# Revit family: Клапан регулирующий ВКТР с аналоговым ВЭП DN15-300, PN16
name_source: partatom
category: Арматура трубопроводов
revit_build: Autodesk Revit 2015 (Build: 20140322_1515(x64)
units: mm (PartAtom-declared; Revit-internal decimal feet)

## types (72) — shared parameters
URL = http://vogez.by
Видимость клапана = Да
Высота болтов площадки = 6 мм
Высота штока_1 = 25 мм
Высота штока_2 = 100 мм
Диаметр направляющих = 10 мм
Диаметр отверстий = 65 мм
Диаметр площадки привода_2 = 35 мм
Диаметр присоединения привода = 40 мм
Диаметр присоединения провода = 15 мм
Диаметр штока_1 = 30 мм
Диаметр штока_2 = 8 мм
Изготовитель = ООО "ВОГЕЗЭНЕРГО"
Максимальная температура среды = 150 °C
Материал и цвет клапана = Чугун, серый
Материал и цвет остальных элементов = Сталь, полированная
Материал и цвет привода = Пластик, чёрный
Наименование = Клапан трёхходовой регулирующий с ЭИМ
Номинальное давление PN = 1.6 МПа
Основание пластины = 20 мм
Рабочая среда = вода
Расстояние до оси привода_1 = 42 мм
Расстояние до оси привода_2 = 133 мм
Сигнал управления = аналоговый
Скругления привода = 25 мм
Степень защиты = IP54
Толщиина пластины = 5 мм
Частота сети = 50 Гц
Ширина пластины = 30 мм
Ширина площадки = 20 мм
Ширина привода = 112 мм

## per-type parameters (varying)
- Клапан регулирующий ВКТР с ЭИМ DN15, Kvy=0.63 м3/ч, 220В: DN=15 мм; Высота клапана=65 мм; Высота направляющих=185 мм; Высота основания привода=195 мм; Высота посадки привода=45 мм; Высота с приводом=265 мм; Диаметр зеркала=51 мм; Диаметр патрубка_1=40 мм; Диаметр патрубка_2=40 мм; Диаметр площадки привода_1=80 мм; Диаметр узла смешивания=70 мм; Диаметр условный DN=15 мм; Диаметр фланца=100 мм; Длина пластины=112 мм; Длина площадки=60 мм; Исполнение ВЭП=1; Масса с приводом=7.00 kg; Межосевое направляющих=65 мм; Напряжение питания=220 В; Номинальное время полного хода ВЭП=63 с; Номинальное усилие ВЭП=1500 Н; Номинальный полный ход ВЭП=20 мм; Обозначение=ВКТР DN15-03 c ЭИМ Kv 0.63; Радиус зеркала=26 мм; Радиус условный=8 мм; Радиус фланца=50 мм; Строительная длина=130 мм; Тип привода=ВЭП-138-1500/63-20; Тип, марка=ВКТР DN15-03 c ЭИМ Kv 0.63; Толщина зеркала=2 мм; Толщина фланца=12 мм; Условная пропускная способность Kvy=0.6 м³/ч; Ход штока=14 мм
- Клапан регулирующий ВКТР с ЭИМ DN15, Kvy=1.25 м3/ч, 220В: DN=15 мм; Высота клапана=65 мм; Высота направляющих=185 мм; Высота основания привода=195 мм; Высота посадки привода=45 мм; Высота с приводом=265 мм; Диаметр зеркала=51 мм; Диаметр патрубка_1=40 мм; Диаметр патрубка_2=40 мм; Диаметр площадки привода_1=80 мм; Диаметр узла смешивания=70 мм; Диаметр условный DN=15 мм; Диаметр фланца=100 мм; Длина пластины=112 мм; Длина площадки=60 мм; Исполнение ВЭП=1; Масса с приводом=7.00 kg; Межосевое направляющих=65 мм; Напряжение питания=220 В; Номинальное время полного хода ВЭП=63 с; Номинальное усилие ВЭП=1500 Н; Номинальный полный ход ВЭП=20 мм; Обозначение=ВКТР DN15-03 c ЭИМ Kv 1.25; Радиус зеркала=26 мм; Радиус условный=8 мм; Радиус фланца=50 мм; Строительная длина=130 мм; Тип привода=ВЭП-138-1500/63-20; Тип, марка=ВКТР DN15-03 c ЭИМ Kv 1.25; Толщина зеркала=2 мм; Толщина фланца=12 мм; Условная пропускная способность Kvy=1.3 м³/ч; Ход штока=14 мм
- Клапан регулирующий ВКТР с ЭИМ DN15, Kvy=1.6 м3/ч, 220В: DN=15 мм; Высота клапана=65 мм; Высота направляющих=185 мм; Высота основания привода=195 мм; Высота посадки привода=45 мм; Высота с приводом=265 мм; Диаметр зеркала=51 мм; Диаметр патрубка_1=40 мм; Диаметр патрубка_2=40 мм; Диаметр площадки привода_1=80 мм; Диаметр узла смешивания=70 мм; Диаметр условный DN=15 мм; Диаметр фланца=100 мм; Длина пластины=112 мм; Длина площадки=60 мм; Исполнение ВЭП=1; Масса с приводом=7.00 kg; Межосевое направляющих=65 мм; Напряжение питания=220 В; Номинальное время полного хода ВЭП=63 с; Номинальное усилие ВЭП=1500 Н; Номинальный полный ход ВЭП=20 мм; Обозначение=ВКТР DN15-03 c ЭИМ Kv 1.6; Радиус зеркала=26 мм; Радиус условный=8 мм; Радиус фланца=50 мм; Строительная длина=130 мм; Тип привода=ВЭП-138-1500/63-20; Тип, марка=ВКТР DN15-03 c ЭИМ Kv 1.6; Толщина зеркала=2 мм; Толщина фланца=12 мм; Условная пропускная способность Kvy=1.6 м³/ч; Ход штока=14 мм
- Клапан регулирующий ВКТР с ЭИМ DN15, Kvy=2.5 м3/ч, 220В: DN=15 мм; Высота клапана=65 мм; Высота направляющих=185 мм; Высота основания привода=195 мм; Высота посадки привода=45 мм; Высота с приводом=265 мм; Диаметр зеркала=51 мм; Диаметр патрубка_1=40 мм; Диаметр патрубка_2=40 мм; Диаметр площадки привода_1=80 мм; Диаметр узла смешивания=70 мм; Диаметр условный DN=15 мм; Диаметр фланца=100 мм; Длина пластины=112 мм; Длина площадки=60 мм; Исполнение ВЭП=1; Масса с приводом=7.00 kg; Межосевое направляющих=65 мм; Напряжение питания=220 В; Номинальное время полного хода ВЭП=63 с; Номинальное усилие ВЭП=1500 Н; Номинальный полный ход ВЭП=20 мм; Обозначение=ВКТР DN15-03 c ЭИМ Kv 2.5; Радиус зеркала=26 мм; Радиус условный=8 мм; Радиус фланца=50 мм; Строительная длина=130 мм; Тип привода=ВЭП-138-1500/63-20; Тип, марка=ВКТР DN15-03 c ЭИМ Kv 2.5; Толщина зеркала=2 мм; Толщина фланца=12 мм; Условная пропускная способность Kvy=2.5 м³/ч; Ход штока=14 мм
- Клапан регулирующий ВКТР с ЭИМ DN15, Kvy=4 м3/ч, 220В: DN=15 мм; Высота клапана=65 мм; Высота направляющих=185 мм; Высота основания привода=195 мм; Высота посадки привода=45 мм; Высота с приводом=265 мм; Диаметр зеркала=51 мм; Диаметр патрубка_1=40 мм; Диаметр патрубка_2=40 мм; Диаметр площадки привода_1=80 мм; Диаметр узла смешивания=70 мм; Диаметр условный DN=15 мм; Диаметр фланца=100 мм; Длина пластины=112 мм; Длина площадки=60 мм; Исполнение ВЭП=1; Масса с приводом=7.00 kg; Межосевое направляющих=65 мм; Напряжение питания=220 В; Номинальное время полного хода ВЭП=63 с; Номинальное усилие ВЭП=1500 Н; Номинальный полный ход ВЭП=20 мм; Обозначение=ВКТР DN15-03 c ЭИМ Kv 4; Радиус зеркала=26 мм; Радиус условный=8 мм; Радиус фланца=50 мм; Строительная длина=130 мм; Тип привода=ВЭП-138-1500/63-20; Тип, марка=ВКТР DN15-03 c ЭИМ Kv 4; Толщина зеркала=2 мм; Толщина фланца=12 мм; Условная пропускная способность Kvy=4.0 м³/ч; Ход штока=14 мм
- Клапан регулирующий ВКТР с ЭИМ DN20, Kvy=5 м3/ч, 220В: DN=20 мм; Высота клапана=70 мм; Высота направляющих=195 мм; Высота основания привода=205 мм; Высота посадки привода=55 мм; Высота с приводом=275 мм; Диаметр зеркала=60 мм; Диаметр патрубка_1=45 мм; Диаметр патрубка_2=40 мм; Диаметр площадки привода_1=80 мм; Диаметр узла смешивания=90 мм; Диаметр условный DN=20 мм; Диаметр фланца=110 мм; Длина пластины=112 мм; Длина площадки=80 мм; Исполнение ВЭП=1; Масса с приводом=8.00 kg; Межосевое направляющих=65 мм; Напряжение питания=220 В; Номинальное время полного хода ВЭП=63 с; Номинальное усилие ВЭП=1500 Н; Номинальный полный ход ВЭП=20 мм; Обозначение=ВКТР DN20-03 c ЭИМ Kv 5; Радиус зеркала=30 мм; Радиус условный=10 мм; Радиус фланца=55 мм; Строительная длина=150 мм; Тип привода=ВЭП-138-1500/63-20; Тип, марка=ВКТР DN20-03 c ЭИМ Kv 5; Толщина зеркала=2 мм; Толщина фланца=14 мм; Условная пропускная способность Kvy=5.0 м³/ч; Ход штока=14 мм
- Клапан регулирующий ВКТР с ЭИМ DN20, Kvy=6.3 м3/ч, 220В: DN=20 мм; Высота клапана=70 мм; Высота направляющих=195 мм; Высота основания привода=205 мм; Высота посадки привода=55 мм; Высота с приводом=275 мм; Диаметр зеркала=60 мм; Диаметр патрубка_1=45 мм; Диаметр патрубка_2=40 мм; Диаметр площадки привода_1=80 мм; Диаметр узла смешивания=90 мм; Диаметр условный DN=20 мм; Диаметр фланца=110 мм; Длина пластины=112 мм; Длина площадки=80 мм; Исполнение ВЭП=1; Масса с приводом=8.00 kg; Межосевое направляющих=65 мм; Напряжение питания=220 В; Номинальное время полного хода ВЭП=63 с; Номинальное усилие ВЭП=1500 Н; Номинальный полный ход ВЭП=20 мм; Обозначение=ВКТР DN20-03 c ЭИМ Kv 6.3; Радиус зеркала=30 мм; Радиус условный=10 мм; Радиус фланца=55 мм; Строительная длина=150 мм; Тип привода=ВЭП-138-1500/63-20; Тип, марка=ВКТР DN20-03 c ЭИМ Kv 6.3; Толщина зеркала=2 мм; Толщина фланца=14 мм; Условная пропускная способность Kvy=6.3 м³/ч; Ход штока=14 мм
- Клапан регулирующий ВКТР с ЭИМ DN25, Kvy=8 м3/ч, 220В: DN=25 мм; Высота клапана=75 мм; Высота направляющих=200 мм; Высота основания привода=210 мм; Высота посадки привода=60 мм; Высота с приводом=280 мм; Диаметр зеркала=71 мм; Диаметр патрубка_1=50 мм; Диаметр патрубка_2=40 мм; Диаметр площадки привода_1=80 мм; Диаметр узла смешивания=100 мм; Диаметр условный DN=25 мм; Диаметр фланца=120 мм; Длина пластины=112 мм; Длина площадки=90 мм; Исполнение ВЭП=1; Масса с приводом=9.00 kg; Межосевое направляющих=65 мм; Напряжение питания=220 В; Номинальное время полного хода ВЭП=63 с; Номинальное усилие ВЭП=1500 Н; Номинальный полный ход ВЭП=20 мм; Обозначение=ВКТР DN25-03 c ЭИМ Kv 8; Радиус зеркала=36 мм; Радиус условный=13 мм; Радиус фланца=60 мм; Строительная длина=160 мм; Тип привода=ВЭП-138-1500/63-20; Тип, марка=ВКТР DN25-03 c ЭИМ Kv 8; Толщина зеркала=2 мм; Толщина фланца=16 мм; Условная пропускная способность Kvy=8.0 м³/ч; Ход штока=14 мм
- Клапан регулирующий ВКТР с ЭИМ DN25, Kvy=10 м3/ч, 220В: DN=25 мм; Высота клапана=75 мм; Высота направляющих=200 мм; Высота основания привода=210 мм; Высота посадки привода=60 мм; Высота с приводом=280 мм; Диаметр зеркала=71 мм; Диаметр патрубка_1=50 мм; Диаметр патрубка_2=40 мм; Диаметр площадки привода_1=80 мм; Диаметр узла смешивания=100 мм; Диаметр условный DN=25 мм; Диаметр фланца=120 мм; Длина пластины=112 мм; Длина площадки=90 мм; Исполнение ВЭП=1; Масса с приводом=9.00 kg; Межосевое направляющих=65 мм; Напряжение питания=220 В; Номинальное время полного хода ВЭП=63 с; Номинальное усилие ВЭП=1500 Н; Номинальный полный ход ВЭП=20 мм; Обозначение=ВКТР DN25-03 c ЭИМ Kv 10; Радиус зеркала=36 мм; Радиус условный=13 мм; Радиус фланца=60 мм; Строительная длина=160 мм; Тип привода=ВЭП-138-1500/63-20; Тип, марка=ВКТР DN25-03 c ЭИМ Kv 10; Толщина зеркала=2 мм; Толщина фланца=16 мм; Условная пропускная способность Kvy=10.0 м³/ч; Ход штока=14 мм
- Клапан регулирующий ВКТР с ЭИМ DN32, Kvy=12.5 м3/ч, 220В: DN=32 мм; Высота клапана=95 мм; Высота направляющих=210 мм; Высота основания привода=220 мм; Высота посадки привода=70 мм; Высота с приводом=290 мм; Диаметр зеркала=82 мм; Диаметр патрубка_1=57 мм; Диаметр патрубка_2=40 мм; Диаметр площадки привода_1=80 мм; Диаметр узла смешивания=120 мм; Диаметр условный DN=32 мм; Диаметр фланца=135 мм; Длина пластины=112 мм; Длина площадки=110 мм; Исполнение ВЭП=1; Масса с приводом=11.00 kg; Межосевое направляющих=65 мм; Напряжение питания=220 В; Номинальное время полного хода ВЭП=63 с; Номинальное усилие ВЭП=1500 Н; Номинальный полный ход ВЭП=20 мм; Обозначение=ВКТР DN32-03 c ЭИМ Kv 12.5; Радиус зеркала=41 мм; Радиус условный=16 мм; Радиус фланца=68 мм; Строительная длина=180 мм; Тип привода=ВЭП-138-1500/63-20; Тип, марка=ВКТР DN32-03 c ЭИМ Kv 12.5; Толщина зеркала=2 мм; Толщина фланца=16 мм; Условная пропускная способность Kvy=12.5 м³/ч; Ход штока=14 мм
- Клапан регулирующий ВКТР с ЭИМ DN32, Kvy=16 м3/ч, 220В: DN=32 мм; Высота клапана=95 мм; Высота направляющих=210 мм; Высота основания привода=220 мм; Высота посадки привода=70 мм; Высота с приводом=290 мм; Диаметр зеркала=82 мм; Диаметр патрубка_1=57 мм; Диаметр патрубка_2=40 мм; Диаметр площадки привода_1=80 мм; Диаметр узла смешивания=120 мм; Диаметр условный DN=32 мм; Диаметр фланца=135 мм; Длина пластины=112 мм; Длина площадки=110 мм; Исполнение ВЭП=1; Масса с приводом=11.00 kg; Межосевое направляющих=65 мм; Напряжение питания=220 В; Номинальное время полного хода ВЭП=63 с; Номинальное усилие ВЭП=1500 Н; Номинальный полный ход ВЭП=20 мм; Обозначение=ВКТР DN32-03 c ЭИМ Kv 16; Радиус зеркала=41 мм; Радиус условный=16 мм; Радиус фланца=68 мм; Строительная длина=180 мм; Тип привода=ВЭП-138-1500/63-20; Тип, марка=ВКТР DN32-03 c ЭИМ Kv 16; Толщина зеркала=2 мм; Толщина фланца=16 мм; Условная пропускная способность Kvy=16.0 м³/ч; Ход штока=14 мм
- Клапан регулирующий ВКТР с ЭИМ DN40, Kvy=20 м3/ч, 220В: DN=40 мм; Высота клапана=100 мм; Высота направляющих=215 мм; Высота основания привода=225 мм; Высота посадки привода=75 мм; Высота с приводом=295 мм; Диаметр зеркала=92 мм; Диаметр патрубка_1=65 мм; Диаметр патрубка_2=60 мм; Диаметр площадки привода_1=80 мм; Диаметр узла смешивания=130 мм; Диаметр условный DN=40 мм; Диаметр фланца=145 мм; Длина пластины=112 мм; Длина площадки=120 мм; Исполнение ВЭП=1; Масса с приводом=13.00 kg; Межосевое направляющих=65 мм; Напряжение питания=220 В; Номинальное время полного хода ВЭП=63 с; Номинальное усилие ВЭП=1500 Н; Номинальный полный ход ВЭП=20 мм; Обозначение=ВКТР DN40-03 c ЭИМ Kv 20; Радиус зеркала=46 мм; Радиус условный=20 мм; Радиус фланца=73 мм; Строительная длина=200 мм; Тип привода=ВЭП-138-1500/63-20; Тип, марка=ВКТР DN40-03 c ЭИМ Kv 20; Толщина зеркала=3 мм; Толщина фланца=17 мм; Условная пропускная способность Kvy=20.0 м³/ч; Ход штока=14 мм
- Клапан регулирующий ВКТР с ЭИМ DN40, Kvy=25 м3/ч, 220В: DN=40 мм; Высота клапана=100 мм; Высота направляющих=215 мм; Высота основания привода=225 мм; Высота посадки привода=75 мм; Высота с приводом=295 мм; Диаметр зеркала=92 мм; Диаметр патрубка_1=65 мм; Диаметр патрубка_2=60 мм; Диаметр площадки привода_1=80 мм; Диаметр узла смешивания=130 мм; Диаметр условный DN=40 мм; Диаметр фланца=145 мм; Длина пластины=112 мм; Длина площадки=120 мм; Исполнение ВЭП=1; Масса с приводом=13.00 kg; Межосевое направляющих=65 мм; Напряжение питания=220 В; Номинальное время полного хода ВЭП=63 с; Номинальное усилие ВЭП=1500 Н; Номинальный полный ход ВЭП=20 мм; Обозначение=ВКТР DN40-03 c ЭИМ Kv 25; Радиус зеркала=46 мм; Радиус условный=20 мм; Радиус фланца=73 мм; Строительная длина=200 мм; Тип привода=ВЭП-138-1500/63-20; Тип, марка=ВКТР DN40-03 c ЭИМ Kv 25; Толщина зеркала=3 мм; Толщина фланца=17 мм; Условная пропускная способность Kvy=25.0 м³/ч; Ход штока=14 мм
- Клапан регулирующий ВКТР с ЭИМ DN50, Kvy=32 м3/ч, 220В: DN=50 мм; Высота клапана=100 мм; Высота направляющих=225 мм; Высота основания привода=235 мм; Высота посадки привода=85 мм; Высота с приводом=305 мм; Диаметр зеркала=107 мм; Диаметр патрубка_1=75 мм; Диаметр патрубка_2=60 мм; Диаметр площадки привода_1=80 мм; Диаметр узла смешивания=150 мм; Диаметр условный DN=50 мм; Диаметр фланца=160 мм; Длина пластины=112 мм; Длина площадки=140 мм; Исполнение ВЭП=1; Масса с приводом=15.00 kg; Межосевое направляющих=65 мм; Напряжение питания=220 В; Номинальное время полного хода ВЭП=63 с; Номинальное усилие ВЭП=1500 Н; Номинальный полный ход ВЭП=20 мм; Обозначение=ВКТР DN50-03 c ЭИМ Kv 32; Радиус зеркала=54 мм; Радиус условный=25 мм; Радиус фланца=80 мм; Строительная длина=230 мм; Тип привода=ВЭП-138-1500/63-20; Тип, марка=ВКТР DN50-03 c ЭИМ Kv 32; Толщина зеркала=3 мм; Толщина фланца=19 мм; Условная пропускная способность Kvy=32.0 м³/ч; Ход штока=14 мм
- Клапан регулирующий ВКТР с ЭИМ DN50, Kvy=40 м3/ч, 220В: DN=50 мм; Высота клапана=100 мм; Высота направляющих=225 мм; Высота основания привода=235 мм; Высота посадки привода=85 мм; Высота с приводом=305 мм; Диаметр зеркала=107 мм; Диаметр патрубка_1=75 мм; Диаметр патрубка_2=60 мм; Диаметр площадки привода_1=80 мм; Диаметр узла смешивания=150 мм; Диаметр условный DN=50 мм; Диаметр фланца=160 мм; Длина пластины=112 мм; Длина площадки=140 мм; Исполнение ВЭП=1; Масса с приводом=15.00 kg; Межосевое направляющих=65 мм; Напряжение питания=220 В; Номинальное время полного хода ВЭП=63 с; Номинальное усилие ВЭП=1500 Н; Номинальный полный ход ВЭП=20 мм; Обозначение=ВКТР DN50-03 c ЭИМ Kv 40; Радиус зеркала=54 мм; Радиус условный=25 мм; Радиус фланца=80 мм; Строительная длина=230 мм; Тип привода=ВЭП-138-1500/63-20; Тип, марка=ВКТР DN50-03 c ЭИМ Kv 40; Толщина зеркала=3 мм; Толщина фланца=19 мм; Условная пропускная способность Kvy=40.0 м³/ч; Ход штока=14 мм
- Клапан регулирующий ВКТР с ЭИМ DN65, Kvy=50 м3/ч, 220В: DN=65 мм; Высота клапана=120 мм; Высота направляющих=285 мм; Высота основания привода=295 мм; Высота посадки привода=115 мм; Высота с приводом=365 мм; Диаметр зеркала=127 мм; Диаметр патрубка_1=90 мм; Диаметр патрубка_2=60 мм; Диаметр площадки привода_1=80 мм; Диаметр узла смешивания=210 мм; Диаметр условный DN=65 мм; Диаметр фланца=180 мм; Длина пластины=112 мм; Длина площадки=200 мм; Исполнение ВЭП=1; Масса с приводом=24.00 kg; Межосевое направляющих=65 мм; Напряжение питания=220 В; Номинальное время полного хода ВЭП=100 с; Номинальное усилие ВЭП=3000 Н; Номинальный полный ход ВЭП=32 мм; Обозначение=ВКТР DN65-03 c ЭИМ Kv 50; Радиус зеркала=64 мм; Радиус условный=33 мм; Радиус фланца=90 мм; Строительная длина=290 мм; Тип привода=ВЭП-138-3000/100-32; Тип, марка=ВКТР DN65-03 c ЭИМ Kv 50; Толщина зеркала=3 мм; Толщина фланца=21 мм; Условная пропускная способность Kvy=50.0 м³/ч; Ход штока=30 мм
- Клапан регулирующий ВКТР с ЭИМ DN65, Kvy=63 м3/ч, 220В: DN=65 мм; Высота клапана=120 мм; Высота направляющих=285 мм; Высота основания привода=295 мм; Высота посадки привода=115 мм; Высота с приводом=365 мм; Диаметр зеркала=127 мм; Диаметр патрубка_1=90 мм; Диаметр патрубка_2=60 мм; Диаметр площадки привода_1=80 мм; Диаметр узла смешивания=210 мм; Диаметр условный DN=65 мм; Диаметр фланца=180 мм; Длина пластины=112 мм; Длина площадки=200 мм; Исполнение ВЭП=1; Масса с приводом=24.00 kg; Межосевое направляющих=65 мм; Напряжение питания=220 В; Номинальное время полного хода ВЭП=100 с; Номинальное усилие ВЭП=3000 Н; Номинальный полный ход ВЭП=32 мм; Обозначение=ВКТР DN65-03 c ЭИМ Kv 63; Радиус зеркала=64 мм; Радиус условный=33 мм; Радиус фланца=90 мм; Строительная длина=290 мм; Тип привода=ВЭП-138-3000/100-32; Тип, марка=ВКТР DN65-03 c ЭИМ Kv 63; Толщина зеркала=3 мм; Толщина фланца=21 мм; Условная пропускная способность Kvy=63.0 м³/ч; Ход штока=30 мм
- Клапан регулирующий ВКТР с ЭИМ DN80, Kvy=80 м3/ч, 220В: DN=80 мм; Высота клапана=130 мм; Высота направляющих=295 мм; Высота основания привода=305 мм; Высота посадки привода=125 мм; Высота с приводом=375 мм; Диаметр зеркала=139 мм; Диаметр патрубка_1=105 мм; Диаметр патрубка_2=60 мм; Диаметр площадки привода_1=80 мм; Диаметр узла смешивания=210 мм; Диаметр условный DN=80 мм; Диаметр фланца=195 мм; Длина пластины=112 мм; Длина площадки=200 мм; Исполнение ВЭП=1; Масса с приводом=28.00 kg; Межосевое направляющих=65 мм; Напряжение питания=220 В; Номинальное время полного хода ВЭП=100 с; Номинальное усилие ВЭП=3000 Н; Номинальный полный ход ВЭП=32 мм; Обозначение=ВКТР DN80-03 c ЭИМ Kv 80; Радиус зеркала=70 мм; Радиус условный=40 мм; Радиус фланца=98 мм; Строительная длина=310 мм; Тип привода=ВЭП-138-3000/100-32; Тип, марка=ВКТР DN80-03 c ЭИМ Kv 80; Толщина зеркала=3 мм; Толщина фланца=21 мм; Условная пропускная способность Kvy=80.0 м³/ч; Ход штока=30 мм
- Клапан регулирующий ВКТР с ЭИМ DN80, Kvy=100 м3/ч, 220В: DN=80 мм; Высота клапана=130 мм; Высота направляющих=295 мм; Высота основания привода=305 мм; Высота посадки привода=125 мм; Высота с приводом=375 мм; Диаметр зеркала=139 мм; Диаметр патрубка_1=105 мм; Диаметр патрубка_2=60 мм; Диаметр площадки привода_1=80 мм; Диаметр узла смешивания=210 мм; Диаметр условный DN=80 мм; Диаметр фланца=195 мм; Длина пластины=112 мм; Длина площадки=200 мм; Исполнение ВЭП=1; Масса с приводом=28.00 kg; Межосевое направляющих=65 мм; Напряжение питания=220 В; Номинальное время полного хода ВЭП=100 с; Номинальное усилие ВЭП=3000 Н; Номинальный полный ход ВЭП=32 мм; Обозначение=ВКТР DN80-03 c ЭИМ Kv 100; Радиус зеркала=70 мм; Радиус условный=40 мм; Радиус фланца=98 мм; Строительная длина=310 мм; Тип привода=ВЭП-138-3000/100-32; Тип, марка=ВКТР DN80-03 c ЭИМ Kv 100; Толщина зеркала=3 мм; Толщина фланца=21 мм; Условная пропускная способность Kvy=100.0 м³/ч; Ход штока=30 мм
- Клапан регулирующий ВКТР с ЭИМ DN100, Kvy=125 м3/ч, 220В: DN=100 мм; Высота клапана=150 мм; Высота направляющих=305 мм; Высота основания привода=315 мм; Высота посадки привода=135 мм; Высота с приводом=385 мм; Диаметр зеркала=162 мм; Диаметр патрубка_1=125 мм; Диаметр патрубка_2=70 мм; Диаметр площадки привода_1=80 мм; Диаметр узла смешивания=230 мм; Диаметр условный DN=100 мм; Диаметр фланца=215 мм; Длина пластины=112 мм; Длина площадки=220 мм; Исполнение ВЭП=1; Масса с приводом=40.00 kg; Межосевое направляющих=65 мм; Напряжение питания=220 В; Номинальное время полного хода ВЭП=100 с; Номинальное усилие ВЭП=3000 Н; Номинальный полный ход ВЭП=32 мм; Обозначение=ВКТР DN100-03 c ЭИМ Kv 125; Радиус зеркала=81 мм; Радиус условный=50 мм; Радиус фланца=108 мм; Строительная длина=350 мм; Тип привода=ВЭП-138-3000/100-32; Тип, марка=ВКТР DN100-03 c ЭИМ Kv 125; Толщина зеркала=3 мм; Толщина фланца=23 мм; Условная пропускная способность Kvy=125.0 м³/ч; Ход штока=30 мм
- Клапан регулирующий ВКТР с ЭИМ DN100, Kvy=160 м3/ч, 220В: DN=100 мм; Высота клапана=150 мм; Высота направляющих=305 мм; Высота основания привода=315 мм; Высота посадки привода=135 мм; Высота с приводом=385 мм; Диаметр зеркала=162 мм; Диаметр патрубка_1=125 мм; Диаметр патрубка_2=70 мм; Диаметр площадки привода_1=80 мм; Диаметр узла смешивания=230 мм; Диаметр условный DN=100 мм; Диаметр фланца=215 мм; Длина пластины=112 мм; Длина площадки=220 мм; Исполнение ВЭП=1; Масса с приводом=40.00 kg; Межосевое направляющих=65 мм; Напряжение питания=220 В; Номинальное время полного хода ВЭП=100 с; Номинальное усилие ВЭП=3000 Н; Номинальный полный ход ВЭП=32 мм; Обозначение=ВКТР DN100-03 c ЭИМ Kv 160; Радиус зеркала=81 мм; Радиус условный=50 мм; Радиус фланца=108 мм; Строительная длина=350 мм; Тип привода=ВЭП-138-3000/100-32; Тип, марка=ВКТР DN100-03 c ЭИМ Kv 160; Толщина зеркала=3 мм; Толщина фланца=23 мм; Условная пропускная способность Kvy=160.0 м³/ч; Ход штока=30 мм
- Клапан регулирующий ВКТР с ЭИМ DN125, Kvy=250 м3/ч, 220В: DN=125 мм; Высота клапана=160 мм; Высота направляющих=390 мм; Высота основания привода=400 мм; Высота посадки привода=90 мм; Высота с приводом=470 мм; Диаметр зеркала=190 мм; Диаметр патрубка_1=150 мм; Диаметр патрубка_2=100 мм; Диаметр площадки привода_1=130 мм; Диаметр узла смешивания=195 мм; Диаметр условный DN=125 мм; Диаметр фланца=245 мм; Длина пластины=130 мм; Длина площадки=185 мм; Исполнение ВЭП=1; Масса с приводом=64.00 kg; Межосевое направляющих=110 мм; Напряжение питания=220 В; Номинальное время полного хода ВЭП=100 с; Номинальное усилие ВЭП=4000 Н; Номинальный полный ход ВЭП=50 мм; Обозначение=ВКТР DN125-03 c ЭИМ Kv 250; Радиус зеркала=95 мм; Радиус условный=63 мм; Радиус фланца=123 мм; Строительная длина=400 мм; Тип привода=ВЭП-138-4000/100-50; Тип, марка=ВКТР DN125-03 c ЭИМ Kv 250; Толщина зеркала=3 мм; Толщина фланца=25 мм; Условная пропускная способность Kvy=250.0 м³/ч; Ход штока=50 мм
- Клапан регулирующий ВКТР с ЭИМ DN150, Kvy=315 м3/ч, 220В: DN=150 мм; Высота клапана=170 мм; Высота направляющих=410 мм; Высота основания привода=420 мм; Высота посадки привода=110 мм; Высота с приводом=490 мм; Диаметр зеркала=218 мм; Диаметр патрубка_1=175 мм; Диаметр патрубка_2=100 мм; Диаметр площадки привода_1=130 мм; Диаметр узла смешивания=235 мм; Диаметр условный DN=150 мм; Диаметр фланца=280 мм; Длина пластины=130 мм; Длина площадки=225 мм; Исполнение ВЭП=1; Масса с приводом=86.00 kg; Межосевое направляющих=110 мм; Напряжение питания=220 В; Номинальное время полного хода ВЭП=100 с; Номинальное усилие ВЭП=4000 Н; Номинальный полный ход ВЭП=50 мм; Обозначение=ВКТР DN150-03 c ЭИМ Kv 315; Радиус зеркала=109 мм; Радиус условный=75 мм; Радиус фланца=140 мм; Строительная длина=480 мм; Тип привода=ВЭП-138-4000/100-50; Тип, марка=ВКТР DN150-03 c ЭИМ Kv 315; Толщина зеркала=3 мм; Толщина фланца=25 мм; Условная пропускная способность Kvy=315.0 м³/ч; Ход штока=50 мм
- Клапан регулирующий ВКТР с ЭИМ DN200, Kvy=315 м3/ч, 220В: DN=200 мм; Высота клапана=400 мм; Высота направляющих=700 мм; Высота основания привода=710 мм; Высота посадки привода=350 мм; Высота с приводом=780 мм; Диаметр зеркала=274 мм; Диаметр патрубка_1=225 мм; Диаметр патрубка_2=100 мм; Диаметр площадки привода_1=130 мм; Диаметр узла смешивания=530 мм; Диаметр условный DN=200 мм; Диаметр фланца=335 мм; Длина пластины=130 мм; Длина площадки=520 мм; Исполнение ВЭП=1; Масса с приводом=240.00 kg; Межосевое направляющих=110 мм; Напряжение питания=220 В; Номинальное время полного хода ВЭП=160 с; Номинальное усилие ВЭП=10000 Н; Номинальный полный ход ВЭП=80 мм; Обозначение=ВКТР DN200-03 c ЭИМ Kv 315; Радиус зеркала=137 мм; Радиус условный=100 мм; Радиус фланца=168 мм; Строительная длина=600 мм; Тип привода=ВЭП-138-10000/160-80; Тип, марка=ВКТР DN200-03 c ЭИМ Kv 315; Толщина зеркала=3 мм; Толщина фланца=27 мм; Условная пропускная способность Kvy=315.0 м³/ч; Ход штока=60 мм
- Клапан регулирующий ВКТР с ЭИМ DN200, Kvy=400 м3/ч, 220В: DN=200 мм; Высота клапана=400 мм; Высота направляющих=700 мм; Высота основания привода=710 мм; Высота посадки привода=350 мм; Высота с приводом=780 мм; Диаметр зеркала=274 мм; Диаметр патрубка_1=225 мм; Диаметр патрубка_2=100 мм; Диаметр площадки привода_1=130 мм; Диаметр узла смешивания=530 мм; Диаметр условный DN=200 мм; Диаметр фланца=335 мм; Длина пластины=130 мм; Длина площадки=520 мм; Исполнение ВЭП=1; Масса с приводом=240.00 kg; Межосевое направляющих=110 мм; Напряжение питания=220 В; Номинальное время полного хода ВЭП=160 с; Номинальное усилие ВЭП=10000 Н; Номинальный полный ход ВЭП=80 мм; Обозначение=ВКТР DN200-03 c ЭИМ Kv 400; Радиус зеркала=137 мм; Радиус условный=100 мм; Радиус фланца=168 мм; Строительная длина=600 мм; Тип привода=ВЭП-138-10000/160-80; Тип, марка=ВКТР DN200-03 c ЭИМ Kv 400; Толщина зеркала=3 мм; Толщина фланца=27 мм; Условная пропускная способность Kvy=400.0 м³/ч; Ход штока=60 мм
- Клапан регулирующий ВКТР с ЭИМ DN200, Kvy=500 м3/ч, 220В: DN=200 мм; Высота клапана=400 мм; Высота направляющих=700 мм; Высота основания привода=710 мм; Высота посадки привода=350 мм; Высота с приводом=780 мм; Диаметр зеркала=274 мм; Диаметр патрубка_1=225 мм; Диаметр патрубка_2=100 мм; Диаметр площадки привода_1=130 мм; Диаметр узла смешивания=530 мм; Диаметр условный DN=200 мм; Диаметр фланца=335 мм; Длина пластины=130 мм; Длина площадки=520 мм; Исполнение ВЭП=1; Масса с приводом=240.00 kg; Межосевое направляющих=110 мм; Напряжение питания=220 В; Номинальное время полного хода ВЭП=160 с; Номинальное усилие ВЭП=10000 Н; Номинальный полный ход ВЭП=80 мм; Обозначение=ВКТР DN200-03 c ЭИМ Kv 500; Радиус зеркала=137 мм; Радиус условный=100 мм; Радиус фланца=168 мм; Строительная длина=600 мм; Тип привода=ВЭП-138-10000/160-80; Тип, марка=ВКТР DN200-03 c ЭИМ Kv 500; Толщина зеркала=3 мм; Толщина фланца=27 мм; Условная пропускная способность Kvy=500.0 м³/ч; Ход штока=60 мм
- Клапан регулирующий ВКТР с ЭИМ DN200, Kvy=630 м3/ч, 220В: DN=200 мм; Высота клапана=400 мм; Высота направляющих=700 мм; Высота основания привода=710 мм; Высота посадки привода=350 мм; Высота с приводом=780 мм; Диаметр зеркала=274 мм; Диаметр патрубка_1=225 мм; Диаметр патрубка_2=100 мм; Диаметр площадки привода_1=130 мм; Диаметр узла смешивания=530 мм; Диаметр условный DN=200 мм; Диаметр фланца=335 мм; Длина пластины=130 мм; Длина площадки=520 мм; Исполнение ВЭП=1; Масса с приводом=240.00 kg; Межосевое направляющих=110 мм; Напряжение питания=220 В; Номинальное время полного хода ВЭП=160 с; Номинальное усилие ВЭП=10000 Н; Номинальный полный ход ВЭП=80 мм; Обозначение=ВКТР DN200-03 c ЭИМ Kv 630; Радиус зеркала=137 мм; Радиус условный=100 мм; Радиус фланца=168 мм; Строительная длина=600 мм; Тип привода=ВЭП-138-10000/160-80; Тип, марка=ВКТР DN200-03 c ЭИМ Kv 630; Толщина зеркала=3 мм; Толщина фланца=27 мм; Условная пропускная способность Kvy=630.0 м³/ч; Ход штока=60 мм
- Клапан регулирующий ВКТР с ЭИМ DN250, Kvy=400 м3/ч, 220В: DN=250 мм; Высота клапана=450 мм; Высота направляющих=750 мм; Высота основания привода=760 мм; Высота посадки привода=400 мм; Высота с приводом=830 мм; Диаметр зеркала=326 мм; Диаметр патрубка_1=275 мм; Диаметр патрубка_2=100 мм; Диаметр площадки привода_1=130 мм; Диаметр узла смешивания=630 мм; Диаметр условный DN=250 мм; Диаметр фланца=405 мм; Длина пластины=130 мм; Длина площадки=620 мм; Исполнение ВЭП=1; Масса с приводом=300.00 kg; Межосевое направляющих=110 мм; Напряжение питания=220 В; Номинальное время полного хода ВЭП=160 с; Номинальное усилие ВЭП=10000 Н; Номинальный полный ход ВЭП=80 мм; Обозначение=ВКТР DN250-03 c ЭИМ Kv 400; Радиус зеркала=163 мм; Радиус условный=125 мм; Радиус фланца=203 мм; Строительная длина=730 мм; Тип привода=ВЭП-138-10000/160-80; Тип, марка=ВКТР DN250-03 c ЭИМ Kv 400; Толщина зеркала=3 мм; Толщина фланца=28 мм; Условная пропускная способность Kvy=400.0 м³/ч; Ход штока=80 мм
- Клапан регулирующий ВКТР с ЭИМ DN250, Kvy=500 м3/ч, 220В: DN=250 мм; Высота клапана=450 мм; Высота направляющих=750 мм; Высота основания привода=760 мм; Высота посадки привода=400 мм; Высота с приводом=830 мм; Диаметр зеркала=326 мм; Диаметр патрубка_1=275 мм; Диаметр патрубка_2=100 мм; Диаметр площадки привода_1=130 мм; Диаметр узла смешивания=630 мм; Диаметр условный DN=250 мм; Диаметр фланца=405 мм; Длина пластины=130 мм; Длина площадки=620 мм; Исполнение ВЭП=1; Масса с приводом=300.00 kg; Межосевое направляющих=110 мм; Напряжение питания=220 В; Номинальное время полного хода ВЭП=160 с; Номинальное усилие ВЭП=10000 Н; Номинальный полный ход ВЭП=80 мм; Обозначение=ВКТР DN250-03 c ЭИМ Kv 500; Радиус зеркала=163 мм; Радиус условный=125 мм; Радиус фланца=203 мм; Строительная длина=730 мм; Тип привода=ВЭП-138-10000/160-80; Тип, марка=ВКТР DN250-03 c ЭИМ Kv 500; Толщина зеркала=3 мм; Толщина фланца=28 мм; Условная пропускная способность Kvy=500.0 м³/ч; Ход штока=80 мм
- Клапан регулирующий ВКТР с ЭИМ DN250, Kvy=630 м3/ч, 220В: DN=250 мм; Высота клапана=450 мм; Высота направляющих=750 мм; Высота основания привода=760 мм; Высота посадки привода=400 мм; Высота с приводом=830 мм; Диаметр зеркала=326 мм; Диаметр патрубка_1=275 мм; Диаметр патрубка_2=100 мм; Диаметр площадки привода_1=130 мм; Диаметр узла смешивания=630 мм; Диаметр условный DN=250 мм; Диаметр фланца=405 мм; Длина пластины=130 мм; Длина площадки=620 мм; Исполнение ВЭП=1; Масса с приводом=300.00 kg; Межосевое направляющих=110 мм; Напряжение питания=220 В; Номинальное время полного хода ВЭП=160 с; Номинальное усилие ВЭП=10000 Н; Номинальный полный ход ВЭП=80 мм; Обозначение=ВКТР DN250-03 c ЭИМ Kv 630; Радиус зеркала=163 мм; Радиус условный=125 мм; Радиус фланца=203 мм; Строительная длина=730 мм; Тип привода=ВЭП-138-10000/160-80; Тип, марка=ВКТР DN250-03 c ЭИМ Kv 630; Толщина зеркала=3 мм; Толщина фланца=28 мм; Условная пропускная способность Kvy=630.0 м³/ч; Ход штока=80 мм
- Клапан регулирующий ВКТР с ЭИМ DN250, Kvy=800 м3/ч, 220В: DN=250 мм; Высота клапана=450 мм; Высота направляющих=750 мм; Высота основания привода=760 мм; Высота посадки привода=400 мм; Высота с приводом=830 мм; Диаметр зеркала=326 мм; Диаметр патрубка_1=275 мм; Диаметр патрубка_2=100 мм; Диаметр площадки привода_1=130 мм; Диаметр узла смешивания=630 мм; Диаметр условный DN=250 мм; Диаметр фланца=405 мм; Длина пластины=130 мм; Длина площадки=620 мм; Исполнение ВЭП=1; Масса с приводом=300.00 kg; Межосевое направляющих=110 мм; Напряжение питания=220 В; Номинальное время полного хода ВЭП=160 с; Номинальное усилие ВЭП=10000 Н; Номинальный полный ход ВЭП=80 мм; Обозначение=ВКТР DN250-03 c ЭИМ Kv 800; Радиус зеркала=163 мм; Радиус условный=125 мм; Радиус фланца=203 мм; Строительная длина=730 мм; Тип привода=ВЭП-138-10000/160-80; Тип, марка=ВКТР DN250-03 c ЭИМ Kv 800; Толщина зеркала=3 мм; Толщина фланца=28 мм; Условная пропускная способность Kvy=800.0 м³/ч; Ход штока=80 мм
- Клапан регулирующий ВКТР с ЭИМ DN250, Kvy=1000 м3/ч, 220В: DN=250 мм; Высота клапана=450 мм; Высота направляющих=750 мм; Высота основания привода=760 мм; Высота посадки привода=400 мм; Высота с приводом=830 мм; Диаметр зеркала=326 мм; Диаметр патрубка_1=275 мм; Диаметр патрубка_2=100 мм; Диаметр площадки привода_1=130 мм; Диаметр узла смешивания=630 мм; Диаметр условный DN=250 мм; Диаметр фланца=405 мм; Длина пластины=130 мм; Длина площадки=620 мм; Исполнение ВЭП=1; Масса с приводом=300.00 kg; Межосевое направляющих=110 мм; Напряжение питания=220 В; Номинальное время полного хода ВЭП=160 с; Номинальное усилие ВЭП=10000 Н; Номинальный полный ход ВЭП=80 мм; Обозначение=ВКТР DN250-03 c ЭИМ Kv 1000; Радиус зеркала=163 мм; Радиус условный=125 мм; Радиус фланца=203 мм; Строительная длина=730 мм; Тип привода=ВЭП-138-10000/160-80; Тип, марка=ВКТР DN250-03 c ЭИМ Kv 1000; Толщина зеркала=3 мм; Толщина фланца=28 мм; Условная пропускная способность Kvy=1000.0 м³/ч; Ход штока=80 мм
- Клапан регулирующий ВКТР с ЭИМ DN300, Kvy=630 м3/ч, 220В: DN=300 мм; Высота клапана=550 мм; Высота направляющих=790 мм; Высота основания привода=800 мм; Высота посадки привода=440 мм; Высота с приводом=870 мм; Диаметр зеркала=378 мм; Диаметр патрубка_1=325 мм; Диаметр патрубка_2=100 мм; Диаметр площадки привода_1=130 мм; Диаметр узла смешивания=710 мм; Диаметр условный DN=300 мм; Диаметр фланца=460 мм; Длина пластины=130 мм; Длина площадки=700 мм; Исполнение ВЭП=1; Масса с приводом=390.00 kg; Межосевое направляющих=110 мм; Напряжение питания=220 В; Номинальное время полного хода ВЭП=160 с; Номинальное усилие ВЭП=10000 Н; Номинальный полный ход ВЭП=80 мм; Обозначение=ВКТР DN300-03 c ЭИМ Kv 630; Радиус зеркала=189 мм; Радиус условный=150 мм; Радиус фланца=230 мм; Строительная длина=850 мм; Тип привода=ВЭП-138-10000/160-80; Тип, марка=ВКТР DN300-03 c ЭИМ Kv 630; Толщина зеркала=4 мм; Толщина фланца=28 мм; Условная пропускная способность Kvy=630.0 м³/ч; Ход штока=80 мм
- Клапан регулирующий ВКТР с ЭИМ DN300, Kvy=800 м3/ч, 220В: DN=300 мм; Высота клапана=550 мм; Высота направляющих=790 мм; Высота основания привода=800 мм; Высота посадки привода=440 мм; Высота с приводом=870 мм; Диаметр зеркала=378 мм; Диаметр патрубка_1=325 мм; Диаметр патрубка_2=100 мм; Диаметр площадки привода_1=130 мм; Диаметр узла смешивания=710 мм; Диаметр условный DN=300 мм; Диаметр фланца=460 мм; Длина пластины=130 мм; Длина площадки=700 мм; Исполнение ВЭП=1; Масса с приводом=390.00 kg; Межосевое направляющих=110 мм; Напряжение питания=220 В; Номинальное время полного хода ВЭП=160 с; Номинальное усилие ВЭП=10000 Н; Номинальный полный ход ВЭП=80 мм; Обозначение=ВКТР DN300-03 c ЭИМ Kv 800; Радиус зеркала=189 мм; Радиус условный=150 мм; Радиус фланца=230 мм; Строительная длина=850 мм; Тип привода=ВЭП-138-10000/160-80; Тип, марка=ВКТР DN300-03 c ЭИМ Kv 800; Толщина зеркала=4 мм; Толщина фланца=28 мм; Условная пропускная способность Kvy=800.0 м³/ч; Ход штока=80 мм
- Клапан регулирующий ВКТР с ЭИМ DN300, Kvy=1000 м3/ч, 220В: DN=300 мм; Высота клапана=550 мм; Высота направляющих=790 мм; Высота основания привода=800 мм; Высота посадки привода=440 мм; Высота с приводом=870 мм; Диаметр зеркала=378 мм; Диаметр патрубка_1=325 мм; Диаметр патрубка_2=100 мм; Диаметр площадки привода_1=130 мм; Диаметр узла смешивания=710 мм; Диаметр условный DN=300 мм; Диаметр фланца=460 мм; Длина пластины=130 мм; Длина площадки=700 мм; Исполнение ВЭП=1; Масса с приводом=390.00 kg; Межосевое направляющих=110 мм; Напряжение питания=220 В; Номинальное время полного хода ВЭП=160 с; Номинальное усилие ВЭП=10000 Н; Номинальный полный ход ВЭП=80 мм; Обозначение=ВКТР DN300-03 c ЭИМ Kv 1000; Радиус зеркала=189 мм; Радиус условный=150 мм; Радиус фланца=230 мм; Строительная длина=850 мм; Тип привода=ВЭП-138-10000/160-80; Тип, марка=ВКТР DN300-03 c ЭИМ Kv 1000; Толщина зеркала=4 мм; Толщина фланца=28 мм; Условная пропускная способность Kvy=1000.0 м³/ч; Ход штока=80 мм
- Клапан регулирующий ВКТР с ЭИМ DN300, Kvy=1250 м3/ч, 220В: DN=300 мм; Высота клапана=550 мм; Высота направляющих=790 мм; Высота основания привода=800 мм; Высота посадки привода=440 мм; Высота с приводом=870 мм; Диаметр зеркала=378 мм; Диаметр патрубка_1=325 мм; Диаметр патрубка_2=100 мм; Диаметр площадки привода_1=130 мм; Диаметр узла смешивания=710 мм; Диаметр условный DN=300 мм; Диаметр фланца=460 мм; Длина пластины=130 мм; Длина площадки=700 мм; Исполнение ВЭП=1; Масса с приводом=390.00 kg; Межосевое направляющих=110 мм; Напряжение питания=220 В; Номинальное время полного хода ВЭП=160 с; Номинальное усилие ВЭП=10000 Н; Номинальный полный ход ВЭП=80 мм; Обозначение=ВКТР DN300-03 c ЭИМ Kv 1250; Радиус зеркала=189 мм; Радиус условный=150 мм; Радиус фланца=230 мм; Строительная длина=850 мм; Тип привода=ВЭП-138-10000/160-80; Тип, марка=ВКТР DN300-03 c ЭИМ Kv 1250; Толщина зеркала=4 мм; Толщина фланца=28 мм; Условная пропускная способность Kvy=1250.0 м³/ч; Ход штока=80 мм
- Клапан регулирующий ВКТР с ЭИМ DN15, Kvy=0.63 м3/ч, 24В: DN=15 мм; Высота клапана=65 мм; Высота направляющих=185 мм; Высота основания привода=195 мм; Высота посадки привода=45 мм; Высота с приводом=265 мм; Диаметр зеркала=51 мм; Диаметр патрубка_1=40 мм; Диаметр патрубка_2=40 мм; Диаметр площадки привода_1=80 мм; Диаметр узла смешивания=70 мм; Диаметр условный DN=15 мм; Диаметр фланца=100 мм; Длина пластины=112 мм; Длина площадки=60 мм; Исполнение ВЭП=2; Масса с приводом=7.00 kg; Межосевое направляющих=65 мм; Напряжение питания=24 В; Номинальное время полного хода ВЭП=63 с; Номинальное усилие ВЭП=1500 Н; Номинальный полный ход ВЭП=20 мм; Обозначение=ВКТР DN15-03 c ЭИМ Kv 0.63; Радиус зеркала=26 мм; Радиус условный=8 мм; Радиус фланца=50 мм; Строительная длина=130 мм; Тип привода=ВЭП-138-1500/63-20; Тип, марка=ВКТР DN15-03 c ЭИМ Kv 0.63; Толщина зеркала=2 мм; Толщина фланца=12 мм; Условная пропускная способность Kvy=0.6 м³/ч; Ход штока=14 мм
- Клапан регулирующий ВКТР с ЭИМ DN100, Kvy=125 м3/ч, 24В: DN=100 мм; Высота клапана=150 мм; Высота направляющих=305 мм; Высота основания привода=315 мм; Высота посадки привода=135 мм; Высота с приводом=385 мм; Диаметр зеркала=162 мм; Диаметр патрубка_1=125 мм; Диаметр патрубка_2=70 мм; Диаметр площадки привода_1=80 мм; Диаметр узла смешивания=230 мм; Диаметр условный DN=100 мм; Диаметр фланца=215 мм; Длина пластины=112 мм; Длина площадки=220 мм; Исполнение ВЭП=2; Масса с приводом=40.00 kg; Межосевое направляющих=65 мм; Напряжение питания=24 В; Номинальное время полного хода ВЭП=100 с; Номинальное усилие ВЭП=3000 Н; Номинальный полный ход ВЭП=32 мм; Обозначение=ВКТР DN100-03 c ЭИМ Kv 125; Радиус зеркала=81 мм; Радиус условный=50 мм; Радиус фланца=108 мм; Строительная длина=350 мм; Тип привода=ВЭП-138-3000/100-32; Тип, марка=ВКТР DN100-03 c ЭИМ Kv 125; Толщина зеркала=3 мм; Толщина фланца=23 мм; Условная пропускная способность Kvy=125.0 м³/ч; Ход штока=30 мм
- Клапан регулирующий ВКТР с ЭИМ DN100, Kvy=160 м3/ч, 24В: DN=100 мм; Высота клапана=150 мм; Высота направляющих=305 мм; Высота основания привода=315 мм; Высота посадки привода=135 мм; Высота с приводом=385 мм; Диаметр зеркала=162 мм; Диаметр патрубка_1=125 мм; Диаметр патрубка_2=70 мм; Диаметр площадки привода_1=80 мм; Диаметр узла смешивания=230 мм; Диаметр условный DN=100 мм; Диаметр фланца=215 мм; Длина пластины=112 мм; Длина площадки=220 мм; Исполнение ВЭП=2; Масса с приводом=40.00 kg; Межосевое направляющих=65 мм; Напряжение питания=24 В; Номинальное время полного хода ВЭП=100 с; Номинальное усилие ВЭП=3000 Н; Номинальный полный ход ВЭП=32 мм; Обозначение=ВКТР DN100-03 c ЭИМ Kv 160; Радиус зеркала=81 мм; Радиус условный=50 мм; Радиус фланца=108 мм; Строительная длина=350 мм; Тип привода=ВЭП-138-3000/100-32; Тип, марка=ВКТР DN100-03 c ЭИМ Kv 160; Толщина зеркала=3 мм; Толщина фланца=23 мм; Условная пропускная способность Kvy=160.0 м³/ч; Ход штока=30 мм
- Клапан регулирующий ВКТР с ЭИМ DN125, Kvy=250 м3/ч, 24В: DN=125 мм; Высота клапана=160 мм; Высота направляющих=390 мм; Высота основания привода=400 мм; Высота посадки привода=90 мм; Высота с приводом=470 мм; Диаметр зеркала=190 мм; Диаметр патрубка_1=150 мм; Диаметр патрубка_2=100 мм; Диаметр площадки привода_1=130 мм; Диаметр узла смешивания=195 мм; Диаметр условный DN=125 мм; Диаметр фланца=245 мм; Длина пластины=130 мм; Длина площадки=185 мм; Исполнение ВЭП=2; Масса с приводом=64.00 kg; Межосевое направляющих=110 мм; Напряжение питания=24 В; Номинальное время полного хода ВЭП=100 с; Номинальное усилие ВЭП=4000 Н; Номинальный полный ход ВЭП=50 мм; Обозначение=ВКТР DN125-03 c ЭИМ Kv 250; Радиус зеркала=95 мм; Радиус условный=63 мм; Радиус фланца=123 мм; Строительная длина=400 мм; Тип привода=ВЭП-138-4000/100-50; Тип, марка=ВКТР DN125-03 c ЭИМ Kv 250; Толщина зеркала=3 мм; Толщина фланца=25 мм; Условная пропускная способность Kvy=250.0 м³/ч; Ход штока=50 мм
- Клапан регулирующий ВКТР с ЭИМ DN15, Kvy=1.25 м3/ч, 24В: DN=15 мм; Высота клапана=65 мм; Высота направляющих=185 мм; Высота основания привода=195 мм; Высота посадки привода=45 мм; Высота с приводом=265 мм; Диаметр зеркала=51 мм; Диаметр патрубка_1=40 мм; Диаметр патрубка_2=40 мм; Диаметр площадки привода_1=80 мм; Диаметр узла смешивания=70 мм; Диаметр условный DN=15 мм; Диаметр фланца=100 мм; Длина пластины=112 мм; Длина площадки=60 мм; Исполнение ВЭП=2; Масса с приводом=7.00 kg; Межосевое направляющих=65 мм; Напряжение питания=24 В; Номинальное время полного хода ВЭП=63 с; Номинальное усилие ВЭП=1500 Н; Номинальный полный ход ВЭП=20 мм; Обозначение=ВКТР DN15-03 c ЭИМ Kv 1.25; Радиус зеркала=26 мм; Радиус условный=8 мм; Радиус фланца=50 мм; Строительная длина=130 мм; Тип привода=ВЭП-138-1500/63-20; Тип, марка=ВКТР DN15-03 c ЭИМ Kv 1.25; Толщина зеркала=2 мм; Толщина фланца=12 мм; Условная пропускная способность Kvy=1.3 м³/ч; Ход штока=14 мм
- Клапан регулирующий ВКТР с ЭИМ DN15, Kvy=1.6 м3/ч, 24В: DN=15 мм; Высота клапана=65 мм; Высота направляющих=185 мм; Высота основания привода=195 мм; Высота посадки привода=45 мм; Высота с приводом=265 мм; Диаметр зеркала=51 мм; Диаметр патрубка_1=40 мм; Диаметр патрубка_2=40 мм; Диаметр площадки привода_1=80 мм; Диаметр узла смешивания=70 мм; Диаметр условный DN=15 мм; Диаметр фланца=100 мм; Длина пластины=112 мм; Длина площадки=60 мм; Исполнение ВЭП=2; Масса с приводом=7.00 kg; Межосевое направляющих=65 мм; Напряжение питания=24 В; Номинальное время полного хода ВЭП=63 с; Номинальное усилие ВЭП=1500 Н; Номинальный полный ход ВЭП=20 мм; Обозначение=ВКТР DN15-03 c ЭИМ Kv 1.6; Радиус зеркала=26 мм; Радиус условный=8 мм; Радиус фланца=50 мм; Строительная длина=130 мм; Тип привода=ВЭП-138-1500/63-20; Тип, марка=ВКТР DN15-03 c ЭИМ Kv 1.6; Толщина зеркала=2 мм; Толщина фланца=12 мм; Условная пропускная способность Kvy=1.6 м³/ч; Ход штока=14 мм
- Клапан регулирующий ВКТР с ЭИМ DN15, Kvy=2.5 м3/ч, 24В: DN=15 мм; Высота клапана=65 мм; Высота направляющих=185 мм; Высота основания привода=195 мм; Высота посадки привода=45 мм; Высота с приводом=265 мм; Диаметр зеркала=51 мм; Диаметр патрубка_1=40 мм; Диаметр патрубка_2=40 мм; Диаметр площадки привода_1=80 мм; Диаметр узла смешивания=70 мм; Диаметр условный DN=15 мм; Диаметр фланца=100 мм; Длина пластины=112 мм; Длина площадки=60 мм; Исполнение ВЭП=2; Масса с приводом=7.00 kg; Межосевое направляющих=65 мм; Напряжение питания=24 В; Номинальное время полного хода ВЭП=63 с; Номинальное усилие ВЭП=1500 Н; Номинальный полный ход ВЭП=20 мм; Обозначение=ВКТР DN15-03 c ЭИМ Kv 2.5; Радиус зеркала=26 мм; Радиус условный=8 мм; Радиус фланца=50 мм; Строительная длина=130 мм; Тип привода=ВЭП-138-1500/63-20; Тип, марка=ВКТР DN15-03 c ЭИМ Kv 2.5; Толщина зеркала=2 мм; Толщина фланца=12 мм; Условная пропускная способность Kvy=2.5 м³/ч; Ход штока=14 мм
- Клапан регулирующий ВКТР с ЭИМ DN15, Kvy=4 м3/ч, 24В: DN=15 мм; Высота клапана=65 мм; Высота направляющих=185 мм; Высота основания привода=195 мм; Высота посадки привода=45 мм; Высота с приводом=265 мм; Диаметр зеркала=51 мм; Диаметр патрубка_1=40 мм; Диаметр патрубка_2=40 мм; Диаметр площадки привода_1=80 мм; Диаметр узла смешивания=70 мм; Диаметр условный DN=15 мм; Диаметр фланца=100 мм; Длина пластины=112 мм; Длина площадки=60 мм; Исполнение ВЭП=2; Масса с приводом=7.00 kg; Межосевое направляющих=65 мм; Напряжение питания=24 В; Номинальное время полного хода ВЭП=63 с; Номинальное усилие ВЭП=1500 Н; Номинальный полный ход ВЭП=20 мм; Обозначение=ВКТР DN15-03 c ЭИМ Kv 4; Радиус зеркала=26 мм; Радиус условный=8 мм; Радиус фланца=50 мм; Строительная длина=130 мм; Тип привода=ВЭП-138-1500/63-20; Тип, марка=ВКТР DN15-03 c ЭИМ Kv 4; Толщина зеркала=2 мм; Толщина фланца=12 мм; Условная пропускная способность Kvy=4.0 м³/ч; Ход штока=14 мм
- Клапан регулирующий ВКТР с ЭИМ DN150, Kvy=315 м3/ч, 24В: DN=150 мм; Высота клапана=170 мм; Высота направляющих=410 мм; Высота основания привода=420 мм; Высота посадки привода=110 мм; Высота с приводом=490 мм; Диаметр зеркала=218 мм; Диаметр патрубка_1=175 мм; Диаметр патрубка_2=100 мм; Диаметр площадки привода_1=130 мм; Диаметр узла смешивания=235 мм; Диаметр условный DN=150 мм; Диаметр фланца=280 мм; Длина пластины=130 мм; Длина площадки=225 мм; Исполнение ВЭП=2; Масса с приводом=86.00 kg; Межосевое направляющих=110 мм; Напряжение питания=24 В; Номинальное время полного хода ВЭП=100 с; Номинальное усилие ВЭП=4000 Н; Номинальный полный ход ВЭП=50 мм; Обозначение=ВКТР DN150-03 c ЭИМ Kv 315; Радиус зеркала=109 мм; Радиус условный=75 мм; Радиус фланца=140 мм; Строительная длина=480 мм; Тип привода=ВЭП-138-4000/100-50; Тип, марка=ВКТР DN150-03 c ЭИМ Kv 315; Толщина зеркала=3 мм; Толщина фланца=25 мм; Условная пропускная способность Kvy=315.0 м³/ч; Ход штока=50 мм
- Клапан регулирующий ВКТР с ЭИМ DN20, Kvy=5 м3/ч, 24В: DN=20 мм; Высота клапана=70 мм; Высота направляющих=195 мм; Высота основания привода=205 мм; Высота посадки привода=55 мм; Высота с приводом=275 мм; Диаметр зеркала=60 мм; Диаметр патрубка_1=45 мм; Диаметр патрубка_2=40 мм; Диаметр площадки привода_1=80 мм; Диаметр узла смешивания=90 мм; Диаметр условный DN=20 мм; Диаметр фланца=110 мм; Длина пластины=112 мм; Длина площадки=80 мм; Исполнение ВЭП=2; Масса с приводом=8.00 kg; Межосевое направляющих=65 мм; Напряжение питания=24 В; Номинальное время полного хода ВЭП=63 с; Номинальное усилие ВЭП=1500 Н; Номинальный полный ход ВЭП=20 мм; Обозначение=ВКТР DN20-03 c ЭИМ Kv 5; Радиус зеркала=30 мм; Радиус условный=10 мм; Радиус фланца=55 мм; Строительная длина=150 мм; Тип привода=ВЭП-138-1500/63-20; Тип, марка=ВКТР DN20-03 c ЭИМ Kv 5; Толщина зеркала=2 мм; Толщина фланца=14 мм; Условная пропускная способность Kvy=5.0 м³/ч; Ход штока=14 мм
- Клапан регулирующий ВКТР с ЭИМ DN20, Kvy=6.3 м3/ч, 24В: DN=20 мм; Высота клапана=70 мм; Высота направляющих=195 мм; Высота основания привода=205 мм; Высота посадки привода=55 мм; Высота с приводом=275 мм; Диаметр зеркала=60 мм; Диаметр патрубка_1=45 мм; Диаметр патрубка_2=40 мм; Диаметр площадки привода_1=80 мм; Диаметр узла смешивания=90 мм; Диаметр условный DN=20 мм; Диаметр фланца=110 мм; Длина пластины=112 мм; Длина площадки=80 мм; Исполнение ВЭП=2; Масса с приводом=8.00 kg; Межосевое направляющих=65 мм; Напряжение питания=24 В; Номинальное время полного хода ВЭП=63 с; Номинальное усилие ВЭП=1500 Н; Номинальный полный ход ВЭП=20 мм; Обозначение=ВКТР DN20-03 c ЭИМ Kv 6.3; Радиус зеркала=30 мм; Радиус условный=10 мм; Радиус фланца=55 мм; Строительная длина=150 мм; Тип привода=ВЭП-138-1500/63-20; Тип, марка=ВКТР DN20-03 c ЭИМ Kv 6.3; Толщина зеркала=2 мм; Толщина фланца=14 мм; Условная пропускная способность Kvy=6.3 м³/ч; Ход штока=14 мм
- Клапан регулирующий ВКТР с ЭИМ DN200, Kvy=315 м3/ч, 24В: DN=200 мм; Высота клапана=400 мм; Высота направляющих=700 мм; Высота основания привода=710 мм; Высота посадки привода=350 мм; Высота с приводом=780 мм; Диаметр зеркала=274 мм; Диаметр патрубка_1=225 мм; Диаметр патрубка_2=100 мм; Диаметр площадки привода_1=130 мм; Диаметр узла смешивания=530 мм; Диаметр условный DN=200 мм; Диаметр фланца=335 мм; Длина пластины=130 мм; Длина площадки=520 мм; Исполнение ВЭП=2; Масса с приводом=240.00 kg; Межосевое направляющих=110 мм; Напряжение питания=24 В; Номинальное время полного хода ВЭП=160 с; Номинальное усилие ВЭП=10000 Н; Номинальный полный ход ВЭП=80 мм; Обозначение=ВКТР DN200-03 c ЭИМ Kv 315; Радиус зеркала=137 мм; Радиус условный=100 мм; Радиус фланца=168 мм; Строительная длина=600 мм; Тип привода=ВЭП-138-10000/160-80; Тип, марка=ВКТР DN200-03 c ЭИМ Kv 315; Толщина зеркала=3 мм; Толщина фланца=27 мм; Условная пропускная способность Kvy=315.0 м³/ч; Ход штока=60 мм
- Клапан регулирующий ВКТР с ЭИМ DN200, Kvy=400 м3/ч, 24В: DN=200 мм; Высота клапана=400 мм; Высота направляющих=700 мм; Высота основания привода=710 мм; Высота посадки привода=350 мм; Высота с приводом=780 мм; Диаметр зеркала=274 мм; Диаметр патрубка_1=225 мм; Диаметр патрубка_2=100 мм; Диаметр площадки привода_1=130 мм; Диаметр узла смешивания=530 мм; Диаметр условный DN=200 мм; Диаметр фланца=335 мм; Длина пластины=130 мм; Длина площадки=520 мм; Исполнение ВЭП=2; Масса с приводом=240.00 kg; Межосевое направляющих=110 мм; Напряжение питания=24 В; Номинальное время полного хода ВЭП=160 с; Номинальное усилие ВЭП=10000 Н; Номинальный полный ход ВЭП=80 мм; Обозначение=ВКТР DN200-03 c ЭИМ Kv 400; Радиус зеркала=137 мм; Радиус условный=100 мм; Радиус фланца=168 мм; Строительная длина=600 мм; Тип привода=ВЭП-138-10000/160-80; Тип, марка=ВКТР DN200-03 c ЭИМ Kv 400; Толщина зеркала=3 мм; Толщина фланца=27 мм; Условная пропускная способность Kvy=400.0 м³/ч; Ход штока=60 мм
- Клапан регулирующий ВКТР с ЭИМ DN200, Kvy=500 м3/ч, 24В: DN=200 мм; Высота клапана=400 мм; Высота направляющих=700 мм; Высота основания привода=710 мм; Высота посадки привода=350 мм; Высота с приводом=780 мм; Диаметр зеркала=274 мм; Диаметр патрубка_1=225 мм; Диаметр патрубка_2=100 мм; Диаметр площадки привода_1=130 мм; Диаметр узла смешивания=530 мм; Диаметр условный DN=200 мм; Диаметр фланца=335 мм; Длина пластины=130 мм; Длина площадки=520 мм; Исполнение ВЭП=2; Масса с приводом=240.00 kg; Межосевое направляющих=110 мм; Напряжение питания=24 В; Номинальное время полного хода ВЭП=160 с; Номинальное усилие ВЭП=10000 Н; Номинальный полный ход ВЭП=80 мм; Обозначение=ВКТР DN200-03 c ЭИМ Kv 500; Радиус зеркала=137 мм; Радиус условный=100 мм; Радиус фланца=168 мм; Строительная длина=600 мм; Тип привода=ВЭП-138-10000/160-80; Тип, марка=ВКТР DN200-03 c ЭИМ Kv 500; Толщина зеркала=3 мм; Толщина фланца=27 мм; Условная пропускная способность Kvy=500.0 м³/ч; Ход штока=60 мм
- Клапан регулирующий ВКТР с ЭИМ DN200, Kvy=630 м3/ч, 24В: DN=200 мм; Высота клапана=400 мм; Высота направляющих=700 мм; Высота основания привода=710 мм; Высота посадки привода=350 мм; Высота с приводом=780 мм; Диаметр зеркала=274 мм; Диаметр патрубка_1=225 мм; Диаметр патрубка_2=100 мм; Диаметр площадки привода_1=130 мм; Диаметр узла смешивания=530 мм; Диаметр условный DN=200 мм; Диаметр фланца=335 мм; Длина пластины=130 мм; Длина площадки=520 мм; Исполнение ВЭП=2; Масса с приводом=240.00 kg; Межосевое направляющих=110 мм; Напряжение питания=24 В; Номинальное время полного хода ВЭП=160 с; Номинальное усилие ВЭП=10000 Н; Номинальный полный ход ВЭП=80 мм; Обозначение=ВКТР DN200-03 c ЭИМ Kv 630; Радиус зеркала=137 мм; Радиус условный=100 мм; Радиус фланца=168 мм; Строительная длина=600 мм; Тип привода=ВЭП-138-10000/160-80; Тип, марка=ВКТР DN200-03 c ЭИМ Kv 630; Толщина зеркала=3 мм; Толщина фланца=27 мм; Условная пропускная способность Kvy=630.0 м³/ч; Ход штока=60 мм
- Клапан регулирующий ВКТР с ЭИМ DN25, Kvy=10 м3/ч, 24В: DN=25 мм; Высота клапана=75 мм; Высота направляющих=200 мм; Высота основания привода=210 мм; Высота посадки привода=60 мм; Высота с приводом=280 мм; Диаметр зеркала=71 мм; Диаметр патрубка_1=50 мм; Диаметр патрубка_2=40 мм; Диаметр площадки привода_1=80 мм; Диаметр узла смешивания=100 мм; Диаметр условный DN=25 мм; Диаметр фланца=120 мм; Длина пластины=112 мм; Длина площадки=90 мм; Исполнение ВЭП=2; Масса с приводом=9.00 kg; Межосевое направляющих=65 мм; Напряжение питания=24 В; Номинальное время полного хода ВЭП=63 с; Номинальное усилие ВЭП=1500 Н; Номинальный полный ход ВЭП=20 мм; Обозначение=ВКТР DN25-03 c ЭИМ Kv 10; Радиус зеркала=36 мм; Радиус условный=13 мм; Радиус фланца=60 мм; Строительная длина=160 мм; Тип привода=ВЭП-138-1500/63-20; Тип, марка=ВКТР DN25-03 c ЭИМ Kv 10; Толщина зеркала=2 мм; Толщина фланца=16 мм; Условная пропускная способность Kvy=10.0 м³/ч; Ход штока=14 мм
- Клапан регулирующий ВКТР с ЭИМ DN25, Kvy=8 м3/ч, 24В: DN=25 мм; Высота клапана=75 мм; Высота направляющих=200 мм; Высота основания привода=210 мм; Высота посадки привода=60 мм; Высота с приводом=280 мм; Диаметр зеркала=71 мм; Диаметр патрубка_1=50 мм; Диаметр патрубка_2=40 мм; Диаметр площадки привода_1=80 мм; Диаметр узла смешивания=100 мм; Диаметр условный DN=25 мм; Диаметр фланца=120 мм; Длина пластины=112 мм; Длина площадки=90 мм; Исполнение ВЭП=2; Масса с приводом=9.00 kg; Межосевое направляющих=65 мм; Напряжение питания=24 В; Номинальное время полного хода ВЭП=63 с; Номинальное усилие ВЭП=1500 Н; Номинальный полный ход ВЭП=20 мм; Обозначение=ВКТР DN25-03 c ЭИМ Kv 8; Радиус зеркала=36 мм; Радиус условный=13 мм; Радиус фланца=60 мм; Строительная длина=160 мм; Тип привода=ВЭП-138-1500/63-20; Тип, марка=ВКТР DN25-03 c ЭИМ Kv 8; Толщина зеркала=2 мм; Толщина фланца=16 мм; Условная пропускная способность Kvy=8.0 м³/ч; Ход штока=14 мм
- Клапан регулирующий ВКТР с ЭИМ DN250, Kvy=1000 м3/ч, 24В: DN=250 мм; Высота клапана=450 мм; Высота направляющих=750 мм; Высота основания привода=760 мм; Высота посадки привода=400 мм; Высота с приводом=830 мм; Диаметр зеркала=326 мм; Диаметр патрубка_1=275 мм; Диаметр патрубка_2=100 мм; Диаметр площадки привода_1=130 мм; Диаметр узла смешивания=630 мм; Диаметр условный DN=250 мм; Диаметр фланца=405 мм; Длина пластины=130 мм; Длина площадки=620 мм; Исполнение ВЭП=2; Масса с приводом=300.00 kg; Межосевое направляющих=110 мм; Напряжение питания=24 В; Номинальное время полного хода ВЭП=160 с; Номинальное усилие ВЭП=10000 Н; Номинальный полный ход ВЭП=80 мм; Обозначение=ВКТР DN250-03 c ЭИМ Kv 1000; Радиус зеркала=163 мм; Радиус условный=125 мм; Радиус фланца=203 мм; Строительная длина=730 мм; Тип привода=ВЭП-138-10000/160-80; Тип, марка=ВКТР DN250-03 c ЭИМ Kv 1000; Толщина зеркала=3 мм; Толщина фланца=28 мм; Условная пропускная способность Kvy=1000.0 м³/ч; Ход штока=80 мм
- Клапан регулирующий ВКТР с ЭИМ DN250, Kvy=400 м3/ч, 24В: DN=250 мм; Высота клапана=450 мм; Высота направляющих=750 мм; Высота основания привода=760 мм; Высота посадки привода=400 мм; Высота с приводом=830 мм; Диаметр зеркала=326 мм; Диаметр патрубка_1=275 мм; Диаметр патрубка_2=100 мм; Диаметр площадки привода_1=130 мм; Диаметр узла смешивания=630 мм; Диаметр условный DN=250 мм; Диаметр фланца=405 мм; Длина пластины=130 мм; Длина площадки=620 мм; Исполнение ВЭП=2; Масса с приводом=300.00 kg; Межосевое направляющих=110 мм; Напряжение питания=24 В; Номинальное время полного хода ВЭП=160 с; Номинальное усилие ВЭП=10000 Н; Номинальный полный ход ВЭП=80 мм; Обозначение=ВКТР DN250-03 c ЭИМ Kv 400; Радиус зеркала=163 мм; Радиус условный=125 мм; Радиус фланца=203 мм; Строительная длина=730 мм; Тип привода=ВЭП-138-10000/160-80; Тип, марка=ВКТР DN250-03 c ЭИМ Kv 400; Толщина зеркала=3 мм; Толщина фланца=28 мм; Условная пропускная способность Kvy=400.0 м³/ч; Ход штока=80 мм
- Клапан регулирующий ВКТР с ЭИМ DN250, Kvy=500 м3/ч, 24В: DN=250 мм; Высота клапана=450 мм; Высота направляющих=750 мм; Высота основания привода=760 мм; Высота посадки привода=400 мм; Высота с приводом=830 мм; Диаметр зеркала=326 мм; Диаметр патрубка_1=275 мм; Диаметр патрубка_2=100 мм; Диаметр площадки привода_1=130 мм; Диаметр узла смешивания=630 мм; Диаметр условный DN=250 мм; Диаметр фланца=405 мм; Длина пластины=130 мм; Длина площадки=620 мм; Исполнение ВЭП=2; Масса с приводом=300.00 kg; Межосевое направляющих=110 мм; Напряжение питания=24 В; Номинальное время полного хода ВЭП=160 с; Номинальное усилие ВЭП=10000 Н; Номинальный полный ход ВЭП=80 мм; Обозначение=ВКТР DN250-03 c ЭИМ Kv 500; Радиус зеркала=163 мм; Радиус условный=125 мм; Радиус фланца=203 мм; Строительная длина=730 мм; Тип привода=ВЭП-138-10000/160-80; Тип, марка=ВКТР DN250-03 c ЭИМ Kv 500; Толщина зеркала=3 мм; Толщина фланца=28 мм; Условная пропускная способность Kvy=500.0 м³/ч; Ход штока=80 мм
- Клапан регулирующий ВКТР с ЭИМ DN250, Kvy=630 м3/ч, 24В: DN=250 мм; Высота клапана=450 мм; Высота направляющих=750 мм; Высота основания привода=760 мм; Высота посадки привода=400 мм; Высота с приводом=830 мм; Диаметр зеркала=326 мм; Диаметр патрубка_1=275 мм; Диаметр патрубка_2=100 мм; Диаметр площадки привода_1=130 мм; Диаметр узла смешивания=630 мм; Диаметр условный DN=250 мм; Диаметр фланца=405 мм; Длина пластины=130 мм; Длина площадки=620 мм; Исполнение ВЭП=2; Масса с приводом=300.00 kg; Межосевое направляющих=110 мм; Напряжение питания=24 В; Номинальное время полного хода ВЭП=160 с; Номинальное усилие ВЭП=10000 Н; Номинальный полный ход ВЭП=80 мм; Обозначение=ВКТР DN250-03 c ЭИМ Kv 630; Радиус зеркала=163 мм; Радиус условный=125 мм; Радиус фланца=203 мм; Строительная длина=730 мм; Тип привода=ВЭП-138-10000/160-80; Тип, марка=ВКТР DN250-03 c ЭИМ Kv 630; Толщина зеркала=3 мм; Толщина фланца=28 мм; Условная пропускная способность Kvy=630.0 м³/ч; Ход штока=80 мм
- Клапан регулирующий ВКТР с ЭИМ DN250, Kvy=800 м3/ч, 24В: DN=250 мм; Высота клапана=450 мм; Высота направляющих=750 мм; Высота основания привода=760 мм; Высота посадки привода=400 мм; Высота с приводом=830 мм; Диаметр зеркала=326 мм; Диаметр патрубка_1=275 мм; Диаметр патрубка_2=100 мм; Диаметр площадки привода_1=130 мм; Диаметр узла смешивания=630 мм; Диаметр условный DN=250 мм; Диаметр фланца=405 мм; Длина пластины=130 мм; Длина площадки=620 мм; Исполнение ВЭП=2; Масса с приводом=300.00 kg; Межосевое направляющих=110 мм; Напряжение питания=24 В; Номинальное время полного хода ВЭП=160 с; Номинальное усилие ВЭП=10000 Н; Номинальный полный ход ВЭП=80 мм; Обозначение=ВКТР DN250-03 c ЭИМ Kv 800; Радиус зеркала=163 мм; Радиус условный=125 мм; Радиус фланца=203 мм; Строительная длина=730 мм; Тип привода=ВЭП-138-10000/160-80; Тип, марка=ВКТР DN250-03 c ЭИМ Kv 800; Толщина зеркала=3 мм; Толщина фланца=28 мм; Условная пропускная способность Kvy=800.0 м³/ч; Ход штока=80 мм
- Клапан регулирующий ВКТР с ЭИМ DN300, Kvy=1000 м3/ч, 24В: DN=300 мм; Высота клапана=550 мм; Высота направляющих=790 мм; Высота основания привода=800 мм; Высота посадки привода=440 мм; Высота с приводом=870 мм; Диаметр зеркала=378 мм; Диаметр патрубка_1=325 мм; Диаметр патрубка_2=100 мм; Диаметр площадки привода_1=130 мм; Диаметр узла смешивания=710 мм; Диаметр условный DN=300 мм; Диаметр фланца=460 мм; Длина пластины=130 мм; Длина площадки=700 мм; Исполнение ВЭП=2; Масса с приводом=390.00 kg; Межосевое направляющих=110 мм; Напряжение питания=24 В; Номинальное время полного хода ВЭП=160 с; Номинальное усилие ВЭП=10000 Н; Номинальный полный ход ВЭП=80 мм; Обозначение=ВКТР DN300-03 c ЭИМ Kv 1000; Радиус зеркала=189 мм; Радиус условный=150 мм; Радиус фланца=230 мм; Строительная длина=850 мм; Тип привода=ВЭП-138-10000/160-80; Тип, марка=ВКТР DN300-03 c ЭИМ Kv 1000; Толщина зеркала=4 мм; Толщина фланца=28 мм; Условная пропускная способность Kvy=1000.0 м³/ч; Ход штока=80 мм
- Клапан регулирующий ВКТР с ЭИМ DN300, Kvy=1250 м3/ч, 24В: DN=300 мм; Высота клапана=550 мм; Высота направляющих=790 мм; Высота основания привода=800 мм; Высота посадки привода=440 мм; Высота с приводом=870 мм; Диаметр зеркала=378 мм; Диаметр патрубка_1=325 мм; Диаметр патрубка_2=100 мм; Диаметр площадки привода_1=130 мм; Диаметр узла смешивания=710 мм; Диаметр условный DN=300 мм; Диаметр фланца=460 мм; Длина пластины=130 мм; Длина площадки=700 мм; Исполнение ВЭП=2; Масса с приводом=390.00 kg; Межосевое направляющих=110 мм; Напряжение питания=24 В; Номинальное время полного хода ВЭП=160 с; Номинальное усилие ВЭП=10000 Н; Номинальный полный ход ВЭП=80 мм; Обозначение=ВКТР DN300-03 c ЭИМ Kv 1250; Радиус зеркала=189 мм; Радиус условный=150 мм; Радиус фланца=230 мм; Строительная длина=850 мм; Тип привода=ВЭП-138-10000/160-80; Тип, марка=ВКТР DN300-03 c ЭИМ Kv 1250; Толщина зеркала=4 мм; Толщина фланца=28 мм; Условная пропускная способность Kvy=1250.0 м³/ч; Ход штока=80 мм
- Клапан регулирующий ВКТР с ЭИМ DN300, Kvy=630 м3/ч, 24В: DN=300 мм; Высота клапана=550 мм; Высота направляющих=790 мм; Высота основания привода=800 мм; Высота посадки привода=440 мм; Высота с приводом=870 мм; Диаметр зеркала=378 мм; Диаметр патрубка_1=325 мм; Диаметр патрубка_2=100 мм; Диаметр площадки привода_1=130 мм; Диаметр узла смешивания=710 мм; Диаметр условный DN=300 мм; Диаметр фланца=460 мм; Длина пластины=130 мм; Длина площадки=700 мм; Исполнение ВЭП=2; Масса с приводом=390.00 kg; Межосевое направляющих=110 мм; Напряжение питания=24 В; Номинальное время полного хода ВЭП=160 с; Номинальное усилие ВЭП=10000 Н; Номинальный полный ход ВЭП=80 мм; Обозначение=ВКТР DN300-03 c ЭИМ Kv 630; Радиус зеркала=189 мм; Радиус условный=150 мм; Радиус фланца=230 мм; Строительная длина=850 мм; Тип привода=ВЭП-138-10000/160-80; Тип, марка=ВКТР DN300-03 c ЭИМ Kv 630; Толщина зеркала=4 мм; Толщина фланца=28 мм; Условная пропускная способность Kvy=630.0 м³/ч; Ход штока=80 мм
- Клапан регулирующий ВКТР с ЭИМ DN300, Kvy=800 м3/ч, 24В: DN=300 мм; Высота клапана=550 мм; Высота направляющих=790 мм; Высота основания привода=800 мм; Высота посадки привода=440 мм; Высота с приводом=870 мм; Диаметр зеркала=378 мм; Диаметр патрубка_1=325 мм; Диаметр патрубка_2=100 мм; Диаметр площадки привода_1=130 мм; Диаметр узла смешивания=710 мм; Диаметр условный DN=300 мм; Диаметр фланца=460 мм; Длина пластины=130 мм; Длина площадки=700 мм; Исполнение ВЭП=2; Масса с приводом=390.00 kg; Межосевое направляющих=110 мм; Напряжение питания=24 В; Номинальное время полного хода ВЭП=160 с; Номинальное усилие ВЭП=10000 Н; Номинальный полный ход ВЭП=80 мм; Обозначение=ВКТР DN300-03 c ЭИМ Kv 800; Радиус зеркала=189 мм; Радиус условный=150 мм; Радиус фланца=230 мм; Строительная длина=850 мм; Тип привода=ВЭП-138-10000/160-80; Тип, марка=ВКТР DN300-03 c ЭИМ Kv 800; Толщина зеркала=4 мм; Толщина фланца=28 мм; Условная пропускная способность Kvy=800.0 м³/ч; Ход штока=80 мм
- Клапан регулирующий ВКТР с ЭИМ DN32, Kvy=12.5 м3/ч, 24В: DN=32 мм; Высота клапана=95 мм; Высота направляющих=210 мм; Высота основания привода=220 мм; Высота посадки привода=70 мм; Высота с приводом=290 мм; Диаметр зеркала=82 мм; Диаметр патрубка_1=57 мм; Диаметр патрубка_2=40 мм; Диаметр площадки привода_1=80 мм; Диаметр узла смешивания=120 мм; Диаметр условный DN=32 мм; Диаметр фланца=135 мм; Длина пластины=112 мм; Длина площадки=110 мм; Исполнение ВЭП=2; Масса с приводом=11.00 kg; Межосевое направляющих=65 мм; Напряжение питания=24 В; Номинальное время полного хода ВЭП=63 с; Номинальное усилие ВЭП=1500 Н; Номинальный полный ход ВЭП=20 мм; Обозначение=ВКТР DN32-03 c ЭИМ Kv 12.5; Радиус зеркала=41 мм; Радиус условный=16 мм; Радиус фланца=68 мм; Строительная длина=180 мм; Тип привода=ВЭП-138-1500/63-20; Тип, марка=ВКТР DN32-03 c ЭИМ Kv 12.5; Толщина зеркала=2 мм; Толщина фланца=16 мм; Условная пропускная способность Kvy=12.5 м³/ч; Ход штока=14 мм
- Клапан регулирующий ВКТР с ЭИМ DN32, Kvy=16 м3/ч, 24В: DN=32 мм; Высота клапана=95 мм; Высота направляющих=210 мм; Высота основания привода=220 мм; Высота посадки привода=70 мм; Высота с приводом=290 мм; Диаметр зеркала=82 мм; Диаметр патрубка_1=57 мм; Диаметр патрубка_2=40 мм; Диаметр площадки привода_1=80 мм; Диаметр узла смешивания=120 мм; Диаметр условный DN=32 мм; Диаметр фланца=135 мм; Длина пластины=112 мм; Длина площадки=110 мм; Исполнение ВЭП=2; Масса с приводом=11.00 kg; Межосевое направляющих=65 мм; Напряжение питания=24 В; Номинальное время полного хода ВЭП=63 с; Номинальное усилие ВЭП=1500 Н; Номинальный полный ход ВЭП=20 мм; Обозначение=ВКТР DN32-03 c ЭИМ Kv 16; Радиус зеркала=41 мм; Радиус условный=16 мм; Радиус фланца=68 мм; Строительная длина=180 мм; Тип привода=ВЭП-138-1500/63-20; Тип, марка=ВКТР DN32-03 c ЭИМ Kv 16; Толщина зеркала=2 мм; Толщина фланца=16 мм; Условная пропускная способность Kvy=16.0 м³/ч; Ход штока=14 мм
- Клапан регулирующий ВКТР с ЭИМ DN40, Kvy=20 м3/ч, 24В: DN=40 мм; Высота клапана=100 мм; Высота направляющих=215 мм; Высота основания привода=225 мм; Высота посадки привода=75 мм; Высота с приводом=295 мм; Диаметр зеркала=92 мм; Диаметр патрубка_1=65 мм; Диаметр патрубка_2=60 мм; Диаметр площадки привода_1=80 мм; Диаметр узла смешивания=130 мм; Диаметр условный DN=40 мм; Диаметр фланца=145 мм; Длина пластины=112 мм; Длина площадки=120 мм; Исполнение ВЭП=2; Масса с приводом=13.00 kg; Межосевое направляющих=65 мм; Напряжение питания=24 В; Номинальное время полного хода ВЭП=63 с; Номинальное усилие ВЭП=1500 Н; Номинальный полный ход ВЭП=20 мм; Обозначение=ВКТР DN40-03 c ЭИМ Kv 20; Радиус зеркала=46 мм; Радиус условный=20 мм; Радиус фланца=73 мм; Строительная длина=200 мм; Тип привода=ВЭП-138-1500/63-20; Тип, марка=ВКТР DN40-03 c ЭИМ Kv 20; Толщина зеркала=3 мм; Толщина фланца=17 мм; Условная пропускная способность Kvy=20.0 м³/ч; Ход штока=14 мм
- Клапан регулирующий ВКТР с ЭИМ DN40, Kvy=25 м3/ч, 24В: DN=40 мм; Высота клапана=100 мм; Высота направляющих=215 мм; Высота основания привода=225 мм; Высота посадки привода=75 мм; Высота с приводом=295 мм; Диаметр зеркала=92 мм; Диаметр патрубка_1=65 мм; Диаметр патрубка_2=60 мм; Диаметр площадки привода_1=80 мм; Диаметр узла смешивания=130 мм; Диаметр условный DN=40 мм; Диаметр фланца=145 мм; Длина пластины=112 мм; Длина площадки=120 мм; Исполнение ВЭП=2; Масса с приводом=13.00 kg; Межосевое направляющих=65 мм; Напряжение питания=24 В; Номинальное время полного хода ВЭП=63 с; Номинальное усилие ВЭП=1500 Н; Номинальный полный ход ВЭП=20 мм; Обозначение=ВКТР DN40-03 c ЭИМ Kv 25; Радиус зеркала=46 мм; Радиус условный=20 мм; Радиус фланца=73 мм; Строительная длина=200 мм; Тип привода=ВЭП-138-1500/63-20; Тип, марка=ВКТР DN40-03 c ЭИМ Kv 25; Толщина зеркала=3 мм; Толщина фланца=17 мм; Условная пропускная способность Kvy=25.0 м³/ч; Ход штока=14 мм
- Клапан регулирующий ВКТР с ЭИМ DN50, Kvy=32 м3/ч, 24В: DN=50 мм; Высота клапана=100 мм; Высота направляющих=225 мм; Высота основания привода=235 мм; Высота посадки привода=85 мм; Высота с приводом=305 мм; Диаметр зеркала=107 мм; Диаметр патрубка_1=75 мм; Диаметр патрубка_2=60 мм; Диаметр площадки привода_1=80 мм; Диаметр узла смешивания=150 мм; Диаметр условный DN=50 мм; Диаметр фланца=160 мм; Длина пластины=112 мм; Длина площадки=140 мм; Исполнение ВЭП=2; Масса с приводом=15.00 kg; Межосевое направляющих=65 мм; Напряжение питания=24 В; Номинальное время полного хода ВЭП=63 с; Номинальное усилие ВЭП=1500 Н; Номинальный полный ход ВЭП=20 мм; Обозначение=ВКТР DN50-03 c ЭИМ Kv 32; Радиус зеркала=54 мм; Радиус условный=25 мм; Радиус фланца=80 мм; Строительная длина=230 мм; Тип привода=ВЭП-138-1500/63-20; Тип, марка=ВКТР DN50-03 c ЭИМ Kv 32; Толщина зеркала=3 мм; Толщина фланца=19 мм; Условная пропускная способность Kvy=32.0 м³/ч; Ход штока=14 мм
- Клапан регулирующий ВКТР с ЭИМ DN50, Kvy=40 м3/ч, 24В: DN=50 мм; Высота клапана=100 мм; Высота направляющих=225 мм; Высота основания привода=235 мм; Высота посадки привода=85 мм; Высота с приводом=305 мм; Диаметр зеркала=107 мм; Диаметр патрубка_1=75 мм; Диаметр патрубка_2=60 мм; Диаметр площадки привода_1=80 мм; Диаметр узла смешивания=150 мм; Диаметр условный DN=50 мм; Диаметр фланца=160 мм; Длина пластины=112 мм; Длина площадки=140 мм; Исполнение ВЭП=2; Масса с приводом=15.00 kg; Межосевое направляющих=65 мм; Напряжение питания=24 В; Номинальное время полного хода ВЭП=63 с; Номинальное усилие ВЭП=1500 Н; Номинальный полный ход ВЭП=20 мм; Обозначение=ВКТР DN50-03 c ЭИМ Kv 40; Радиус зеркала=54 мм; Радиус условный=25 мм; Радиус фланца=80 мм; Строительная длина=230 мм; Тип привода=ВЭП-138-1500/63-20; Тип, марка=ВКТР DN50-03 c ЭИМ Kv 40; Толщина зеркала=3 мм; Толщина фланца=19 мм; Условная пропускная способность Kvy=40.0 м³/ч; Ход штока=14 мм
- Клапан регулирующий ВКТР с ЭИМ DN65, Kvy=50 м3/ч, 24В: DN=65 мм; Высота клапана=120 мм; Высота направляющих=285 мм; Высота основания привода=295 мм; Высота посадки привода=115 мм; Высота с приводом=365 мм; Диаметр зеркала=127 мм; Диаметр патрубка_1=90 мм; Диаметр патрубка_2=60 мм; Диаметр площадки привода_1=80 мм; Диаметр узла смешивания=210 мм; Диаметр условный DN=65 мм; Диаметр фланца=180 мм; Длина пластины=112 мм; Длина площадки=200 мм; Исполнение ВЭП=2; Масса с приводом=24.00 kg; Межосевое направляющих=65 мм; Напряжение питания=24 В; Номинальное время полного хода ВЭП=100 с; Номинальное усилие ВЭП=3000 Н; Номинальный полный ход ВЭП=32 мм; Обозначение=ВКТР DN65-03 c ЭИМ Kv 50; Радиус зеркала=64 мм; Радиус условный=33 мм; Радиус фланца=90 мм; Строительная длина=290 мм; Тип привода=ВЭП-138-3000/100-32; Тип, марка=ВКТР DN65-03 c ЭИМ Kv 50; Толщина зеркала=3 мм; Толщина фланца=21 мм; Условная пропускная способность Kvy=50.0 м³/ч; Ход штока=30 мм
- Клапан регулирующий ВКТР с ЭИМ DN65, Kvy=63 м3/ч, 24В: DN=65 мм; Высота клапана=120 мм; Высота направляющих=285 мм; Высота основания привода=295 мм; Высота посадки привода=115 мм; Высота с приводом=365 мм; Диаметр зеркала=127 мм; Диаметр патрубка_1=90 мм; Диаметр патрубка_2=60 мм; Диаметр площадки привода_1=80 мм; Диаметр узла смешивания=210 мм; Диаметр условный DN=65 мм; Диаметр фланца=180 мм; Длина пластины=112 мм; Длина площадки=200 мм; Исполнение ВЭП=2; Масса с приводом=24.00 kg; Межосевое направляющих=65 мм; Напряжение питания=24 В; Номинальное время полного хода ВЭП=100 с; Номинальное усилие ВЭП=3000 Н; Номинальный полный ход ВЭП=32 мм; Обозначение=ВКТР DN65-03 c ЭИМ Kv 63; Радиус зеркала=64 мм; Радиус условный=33 мм; Радиус фланца=90 мм; Строительная длина=290 мм; Тип привода=ВЭП-138-3000/100-32; Тип, марка=ВКТР DN65-03 c ЭИМ Kv 63; Толщина зеркала=3 мм; Толщина фланца=21 мм; Условная пропускная способность Kvy=63.0 м³/ч; Ход штока=30 мм
- Клапан регулирующий ВКТР с ЭИМ DN80, Kvy=100 м3/ч, 24В: DN=80 мм; Высота клапана=130 мм; Высота направляющих=295 мм; Высота основания привода=305 мм; Высота посадки привода=125 мм; Высота с приводом=375 мм; Диаметр зеркала=139 мм; Диаметр патрубка_1=105 мм; Диаметр патрубка_2=60 мм; Диаметр площадки привода_1=80 мм; Диаметр узла смешивания=210 мм; Диаметр условный DN=80 мм; Диаметр фланца=195 мм; Длина пластины=112 мм; Длина площадки=200 мм; Исполнение ВЭП=2; Масса с приводом=28.00 kg; Межосевое направляющих=65 мм; Напряжение питания=24 В; Номинальное время полного хода ВЭП=100 с; Номинальное усилие ВЭП=3000 Н; Номинальный полный ход ВЭП=32 мм; Обозначение=ВКТР DN80-03 c ЭИМ Kv 100; Радиус зеркала=70 мм; Радиус условный=40 мм; Радиус фланца=98 мм; Строительная длина=310 мм; Тип привода=ВЭП-138-3000/100-32; Тип, марка=ВКТР DN80-03 c ЭИМ Kv 100; Толщина зеркала=3 мм; Толщина фланца=21 мм; Условная пропускная способность Kvy=100.0 м³/ч; Ход штока=30 мм
- Клапан регулирующий ВКТР с ЭИМ DN80, Kvy=80 м3/ч, 24В: DN=80 мм; Высота клапана=130 мм; Высота направляющих=295 мм; Высота основания привода=305 мм; Высота посадки привода=125 мм; Высота с приводом=375 мм; Диаметр зеркала=139 мм; Диаметр патрубка_1=105 мм; Диаметр патрубка_2=60 мм; Диаметр площадки привода_1=80 мм; Диаметр узла смешивания=210 мм; Диаметр условный DN=80 мм; Диаметр фланца=195 мм; Длина пластины=112 мм; Длина площадки=200 мм; Исполнение ВЭП=2; Масса с приводом=28.00 kg; Межосевое направляющих=65 мм; Напряжение питания=24 В; Номинальное время полного хода ВЭП=100 с; Номинальное усилие ВЭП=3000 Н; Номинальный полный ход ВЭП=32 мм; Обозначение=ВКТР DN80-03 c ЭИМ Kv 80; Радиус зеркала=70 мм; Радиус условный=40 мм; Радиус фланца=98 мм; Строительная длина=310 мм; Тип привода=ВЭП-138-3000/100-32; Тип, марка=ВКТР DN80-03 c ЭИМ Kv 80; Толщина зеркала=3 мм; Толщина фланца=21 мм; Условная пропускная способность Kvy=80.0 м³/ч; Ход штока=30 мм
